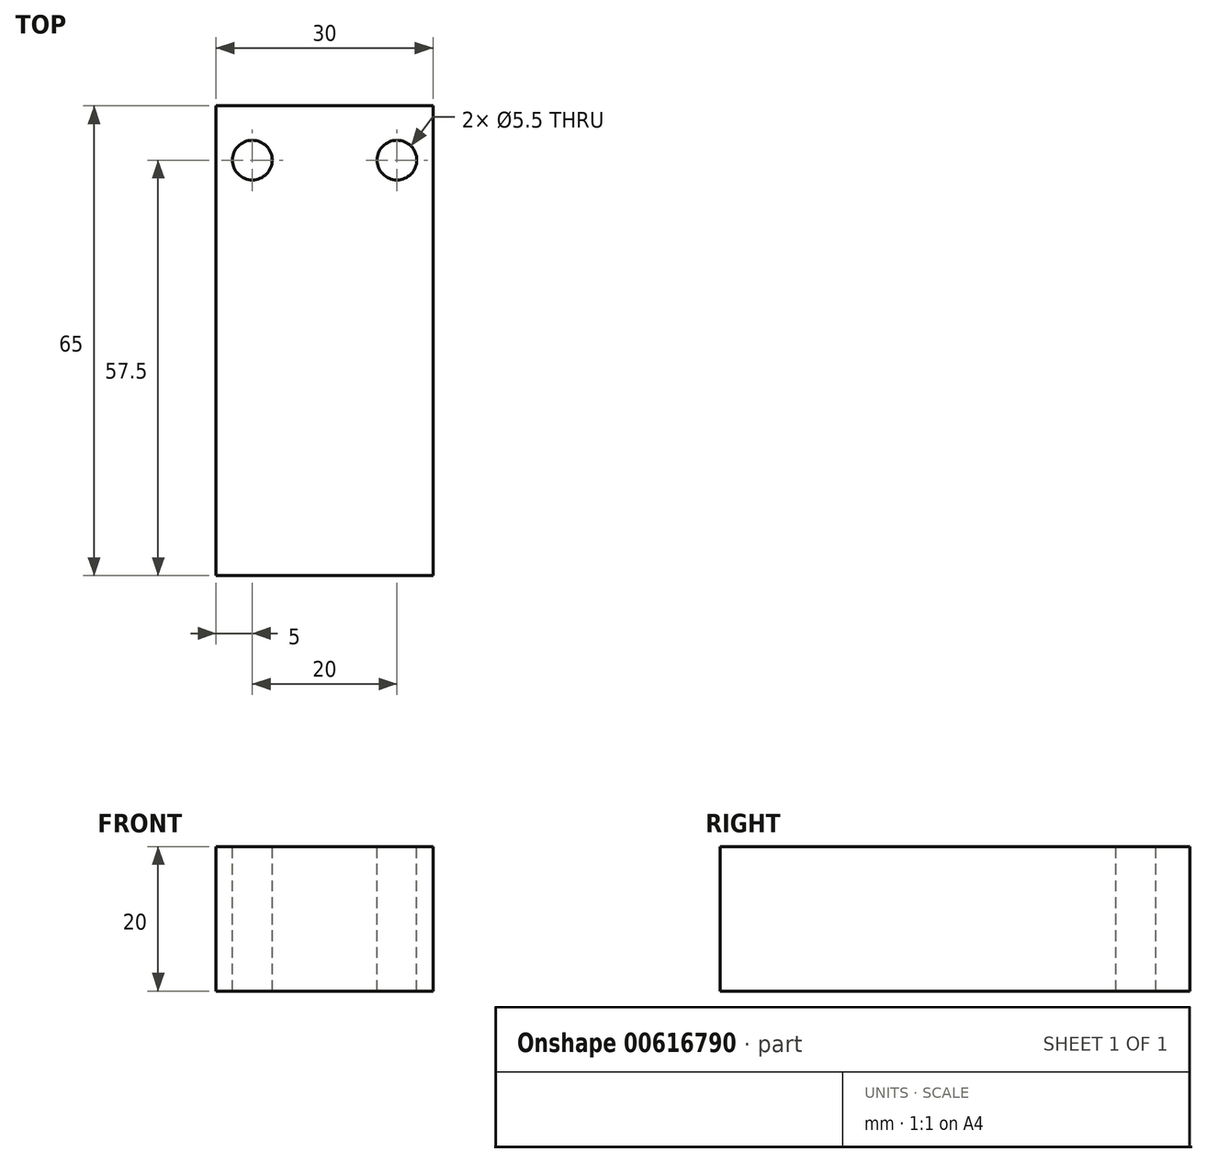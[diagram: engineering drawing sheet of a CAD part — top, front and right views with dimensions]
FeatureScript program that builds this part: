
annotation { "Feature Type Name" : "Feature", "Feature Type Description" : "" }
export const myFeature = defineFeature(function(context is Context, id is Id, definition is map)
    precondition{}
    {
        {
            var Q0;
            Q0=qCreatedBy(makeId("Top.planeOp"),FACE);
            var sketch = newSketch(context, id + "F0", { "sketchPlane" : qUnion([Q0])});
            skLineSegment(sketch, "E0.bottom", {"start": v(15, 32.5) * mm, "end": v(-15, 32.5) * mm});
            skLineSegment(sketch, "E0.top", {"start": v(15, -32.5) * mm, "end": v(-15, -32.5) * mm});
            skLineSegment(sketch, "E0.left", {"start": v(15, 32.5) * mm, "end": v(15, -32.5) * mm});
            skLineSegment(sketch, "E0.right", {"start": v(-15, 32.5) * mm, "end": v(-15, -32.5) * mm});
            skPoint(sketch, "E0.middle", {"position": v(0, 0) * mm});
            skPoint(sketch, "E1", {"position": v(-10, 25) * mm});
            skPoint(sketch, "E2", {"position": v(10, 25) * mm});
            skSolve(sketch);
        }
        {
            var Q0;
            Q0 = qSketchRegion(id + "F0", true);
            extrude(context, id + "F1", {"entities" : qUnion([Q0]), "depth" : 20 * mm, "offsetDistance" : 25 * mm});
        }
        {
            var Q0;
            Q0=sQuery(id+"F0.wireOp",VERTEX,"E1");
            var Q1;
            Q1=sQuery(id+"F0.wireOp",VERTEX,"E2");
            var Q2;
            Q2=makeQuery(id+"F1.opExtrude","SWEPT_BODY",BODY,{"disambiguationData":[OSD([sQuery(id+"F0.wireOp",EDGE,"E0.bottom"),sQuery(id+"F0.wireOp",EDGE,"E0.top"),sQuery(id+"F0.wireOp",EDGE,"E0.left"),sQuery(id+"F0.wireOp",EDGE,"E0.right")])]});
            hole(context, id + "F2", {"style" : HoleStyle.SIMPLE, "endStyle" : HoleEndStyle.THROUGH, "oppositeDirection" : true, "standardTappedOrClearance" : lookupTablePath({ "fit" : "Normal", "standard" : "ISO", "size" : "M5", "type" : "Clearance" }), "standardBlindInLast" : lookupTablePath({ "fit" : "Normal", "standard" : "ISO", "size" : "M5", "type" : "Clearance" }), "holeDiameter" : 5.5 * mm, "majorDiameter" : 5 * mm, "isTappedThrough" : true, "tappedDepth" : 3.9 * mm, "tapClearance" : 3, "locations" : qUnion([Q0, Q1]), "scope" : qUnion([Q2]), "startStyle" : HoleStartStyle.PART});
        }
    });
